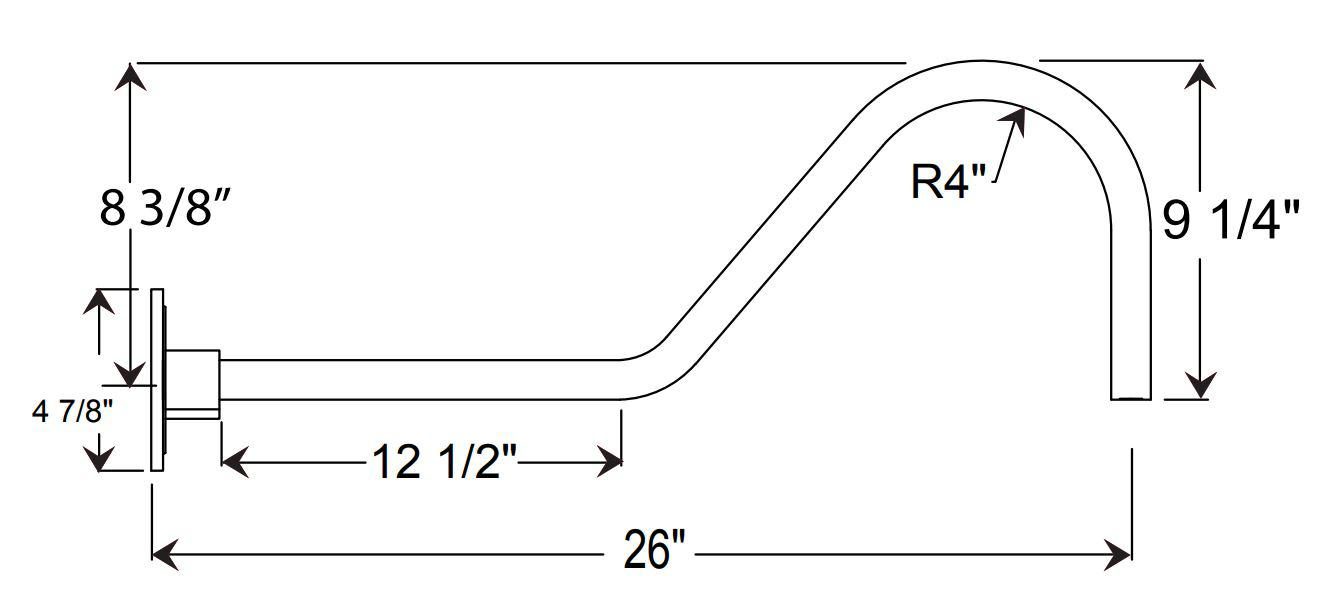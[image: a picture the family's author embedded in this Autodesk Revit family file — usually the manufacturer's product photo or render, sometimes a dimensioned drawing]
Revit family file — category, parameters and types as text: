
# Revit family: OSUL LED 38
name_source: partatom
category: Lighting Fixtures
units: mm (PartAtom-declared; Revit-internal decimal feet)

## family parameters
Always vertical = Yes
Cut with Voids When Loaded = No
Light Source = Yes
OmniClass Number = 23.80.70.00
OmniClass Title = Lighting
Part Type = Normal
Room Calculation Point = No
Round Connector Dimension = Use Diameter
Shared = No
Work Plane-Based = No

## types (1)
- OSUL38
    Apparent Load = 37 VA
    Body Colour = Spun aluminium
    Body Material = body
    Bulb = Glass
    CRI = >90
    Canopy Body = body
    Color Filter = 16777215
    Construction Material = Heavy Duty spun aluminum.
    Default Elevation = 0' - 0"
    Description = 120-277 Voltage
    Dimming = 1%
    Dimming Lamp Color Temperature Shift = <None>
    Efficiency = 65-125 lumens per watt
    Fixture Diameter = 3' - 2"
    Fixture Height = 2' - 11"
    INSIDE BODY = Default
    Lamp = LED
    Life = L70 50,000 hours
    Load Classification = Lighting
    Manufacturer = ANP Lighting
    Model = OSUL38
    OSUL38 = Yes
    Photometric Web File = OSUL38M037LDNW40K.IES
    Power Factor = 1
    Tilt Angle = 90.00°
    URL = https://www.anplighting.com
    Voltage = 120 V
    Warranty = 5 year limited warranty
    Wattage Comments = 37 W
    Weight = 17.0 lbs
    a = 2' - 4"
    b = 0' - 2"

## geometry (parser evidence)
native form markers: Sweep x19
no freeform markers — native parametric forms only
